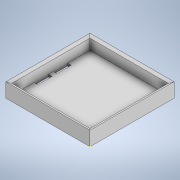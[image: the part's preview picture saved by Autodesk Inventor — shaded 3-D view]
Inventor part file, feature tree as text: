
AUTODESK INVENTOR PART (.ipt)
format: ipt  version: 2021 (Build 250183000, 183)  size: 161,792 bytes
history: native  units: in
note: dims shown in document units (in); Inventor stores cm internally (conversion verified against a paired STEP export)
features: sketch x4, chamfer x4, extrude x3, projected_geometry x2
ambient origin geometry x8: Origin, YZ Plane, XZ Plane, XY Plane, X Axis, Y Axis, Z Axis, Center Point
bodies: Solid1 (feature_tree)
feature tree (13):
  sketch  "Sketch1"  dims[d0=1.3858in d1=1.3858in]
  extrude  "Extrusion1"  Depth=1.3858in
  extrude  "Extrusion2"  Depth=0.0472in
  extrude  "Extrusion3"  Depth=1.2913in
  chamfer  "Chamfer3"  Distance=0.1969in
  chamfer  "Chamfer4"  Distance=0.0394in
  chamfer  "Chamfer5"  Distance=0.0591in
  chamfer  "Chamfer6"  Distance=0.2362in
  sketch  "Sketch2"  dims[d2=0.0394in d3=0.0in d4=0.0472in]
  sketch  "Sketch3"  dims[d5=0.0472in d6=1.2913in]
  projected_geometry  "Projected Loop1"
  sketch  "Sketch4"  dims[d7=1.2913in d8=0.1969in d9=0.0in d13=0.0394in d19=0.0591in d20=0.2362in d21=0.1575in d22=0.0in d37=0.0472in d38=0.0236in d39=45.0deg d40=0.0472in d41=0.0236in d42=45.0deg d43=0.0472in d44=0.0236in d45=45.0deg d46=0.0472in d47=0.0236in d48=45.0deg d49=0.2362in]
  projected_geometry  "Projected Loop2"
